# Revit family: V61A-45U-600x1000mm-26.03.14
name_source: partatom
category: Electrical Equipment
revit_build: Autodesk Revit 2013 (Build: 20120221_2030(x64)
units: mm (PartAtom-declared; Revit-internal decimal feet)

## types (2) — shared parameters
Color = BLACK
Item Class = 1F
Item Group = RACKS
Manufacturer = SIEMON
Segment = CSS
System = VPOD
U Space = 45
U/M = EA
Weight = 0.00 lb
zero-valued in all types: Ports

## per-type parameters (varying)
| type | Cabinet Depth | Cabinet Height | Cabinet Width Overall | Description | Door Back | Door Construction Back | Door Construction Front | Door Construction Side | Door Front | Lock | Metal | Model | Mounting Rail Material | Mounting rail 45 U | Serial Number | Side Panel Left | Side Panel Right | Usable Depth |
| Server_Rack-Siemon-600mm | 1000 mm  [stored 3.28084 ft] | 2150 mm | 600 mm | WARNING: PLEASE RELOAD FAMILY USING THE TYPE CATALOG | No |  |  | 0 | No |  | SIEMON STEEL | V61A | SIEMON STEEL | SIEMON STEEL |  | No | No | 806 mm |
| V1-2AB211 | 1090 mm | 2140 mm | 605 mm | VPOD,600x1000,S-PNL(2),F-DR FL VNT,R-DR SP VNT,TUM,T-PNL BLANK,BLK | Yes | SPLIT VENTED | FULL VENTED | 2 | Yes | COMBINATION | Metal-Siemon-Frame_Metal | VERSPOD | Metal-Siemon-Annodized-Aluminum | Metal-Siemon-Annodized-Aluminum | V1-2AB211 | Yes | Yes | 0 mm  [stored 0 ft] |

note: [stored X ft] marks values corroborated as IEEE doubles in the binary element streams (Revit-internal decimal feet)

## geometry (parser evidence)
native form markers: Blend x8, Sweep x8
no freeform markers — native parametric forms only
